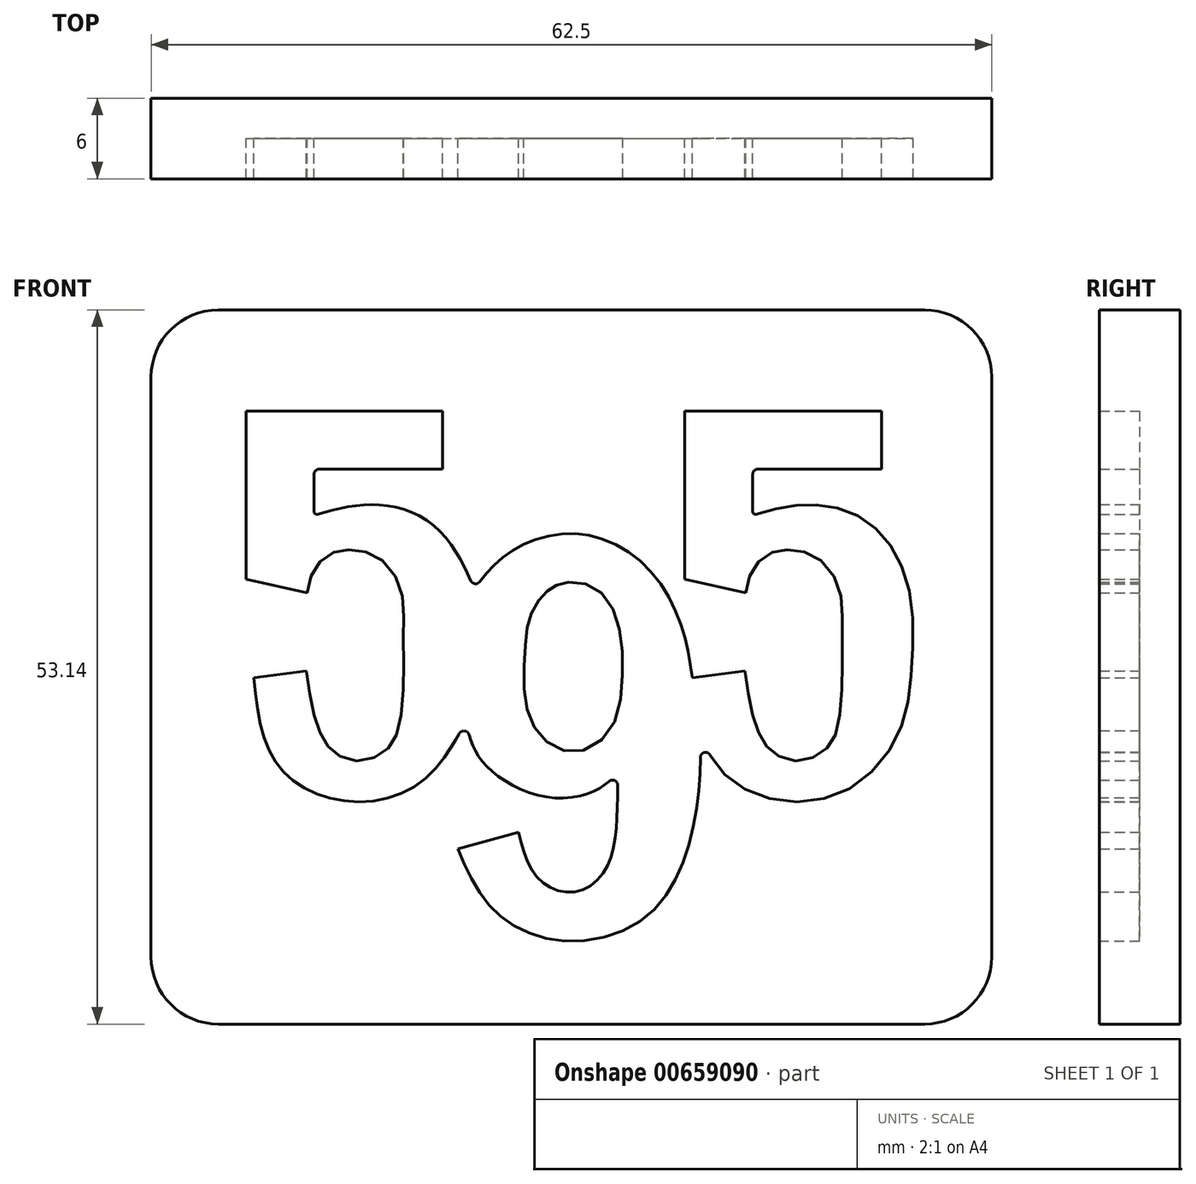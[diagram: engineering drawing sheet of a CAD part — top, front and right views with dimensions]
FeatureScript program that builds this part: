
annotation { "Feature Type Name" : "Feature", "Feature Type Description" : "" }
export const myFeature = defineFeature(function(context is Context, id is Id, definition is map)
    precondition{}
    {
        {
            var Q0;
            Q0=qCreatedBy(makeId("Front.planeOp"),FACE);
            var sketch = newSketch(context, id + "F0", { "sketchPlane" : qUnion([Q0])});
            skLineSegment(sketch, "E0", {"start": v(-24.18, 19.03) * mm, "end": v(-9.57, 19.03) * mm});
            skLineSegment(sketch, "E1", {"start": v(-24.18, 19.03) * mm, "end": v(-24.18, 6.52) * mm});
            skLineSegment(sketch, "E2", {"start": v(-24.18, 6.52) * mm, "end": v(-19.64, 5.52) * mm});
            skLineSegment(sketch, "E3", {"start": v(-9.57, 19.03) * mm, "end": v(-9.57, 14.73) * mm});
            skLineSegment(sketch, "E4", {"start": v(-9.57, 14.73) * mm, "end": v(-18.75, 14.73) * mm});
            skLineSegment(sketch, "E5", {"start": v(-19.13, 14.34) * mm, "end": v(-19.13, 11.56) * mm});
            skLineSegment(sketch, "E6", {"start": v(-19.7, -0.28) * mm, "end": v(-23.62, -0.8) * mm});
            skLineSegment(sketch, "E7", {"start": v(8.43, 19.03) * mm, "end": v(23.04, 19.03) * mm});
            skLineSegment(sketch, "E8", {"start": v(8.43, 19.03) * mm, "end": v(8.43, 6.52) * mm});
            skLineSegment(sketch, "E9", {"start": v(8.43, 6.52) * mm, "end": v(12.97, 5.52) * mm});
            skLineSegment(sketch, "E10", {"start": v(23.04, 19.03) * mm, "end": v(23.04, 14.73) * mm});
            skLineSegment(sketch, "E11", {"start": v(23.04, 14.73) * mm, "end": v(13.87, 14.73) * mm});
            skLineSegment(sketch, "E12", {"start": v(13.48, 14.34) * mm, "end": v(13.48, 11.56) * mm});
            skLineSegment(sketch, "E13", {"start": v(12.9, -0.28) * mm, "end": v(8.99, -0.8) * mm});
            skFitSpline(sketch, "E14", {"points": [v(-23.62, -0.8) * mm, v(-22.6, -5.93) * mm, v(-20.1, -8.86) * mm, v(-15.7, -10.03) * mm, v(-11.16, -8.56) * mm, v(-8.72, -5.62) * mm, v(-8.17, -4.64) * mm], "startDerivative": vector(3.05, -27.84) * mm, "endDerivative": vector(4.84, 9.1) * mm});
            skFitSpline(sketch, "E15", {"points": [v(-19.7, -0.28) * mm, v(-19.17, -3.5) * mm, v(-18.4, -5.44) * mm, v(-17.3, -6.6) * mm, v(-15.43, -6.96) * mm, v(-13.7, -6.12) * mm, v(-12.88, -4.67) * mm, v(-12.49, -0.89) * mm, v(-12.49, 3.08) * mm, v(-12.67, 5.78) * mm, v(-14.23, 8.06) * mm, v(-16.23, 8.7) * mm, v(-17.75, 8.5) * mm, v(-19.11, 7.28) * mm, v(-19.64, 5.52) * mm], "startDerivative": vector(5.37, -39.95) * mm, "endDerivative": vector(-5.42, -28.28) * mm});
            skFitSpline(sketch, "E16", {"points": [v(-19.13, 11.3) * mm, v(-16.5, 11.94) * mm, v(-13.79, 12) * mm, v(-10.94, 11.04) * mm, v(-8.67, 8.72) * mm, v(-7.35, 6.14) * mm], "startDerivative": vector(13.56, 3.87) * mm, "endDerivative": vector(5.77, -13.07) * mm});
            skFitSpline(sketch, "E17", {"points": [v(12.9, -0.28) * mm, v(13.45, -3.5) * mm, v(14.2, -5.44) * mm, v(15.31, -6.6) * mm, v(17.18, -6.96) * mm, v(18.92, -6.12) * mm, v(19.73, -4.67) * mm, v(20.13, -0.89) * mm, v(20.13, 3.08) * mm, v(19.94, 5.78) * mm, v(18.38, 8.06) * mm, v(16.39, 8.7) * mm, v(14.87, 8.5) * mm, v(13.5, 7.28) * mm, v(12.97, 5.52) * mm], "startDerivative": vector(5.37, -39.95) * mm, "endDerivative": vector(-5.42, -28.28) * mm});
            skFitSpline(sketch, "E18", {"points": [v(13.48, 11.3) * mm, v(16.1, 11.94) * mm, v(18.82, 12) * mm, v(21.67, 11.04) * mm, v(23.94, 8.72) * mm, v(25.26, 4.86) * mm, v(25.26, -0.53) * mm, v(24.45, -4.64) * mm, v(21.45, -8.56) * mm, v(16.92, -10.03) * mm, v(12.52, -8.86) * mm, v(10, -5.93) * mm, v(8.99, -0.8) * mm], "startDerivative": vector(38.15, 10.87) * mm, "endDerivative": vector(-6.34, 57.7) * mm});
            skFitSpline(sketch, "E19", {"points": [v(-6.99, 6.14) * mm, v(-5.14, 8.11) * mm, v(-2.12, 9.65) * mm, v(1.76, 9.7) * mm, v(5.68, 7.36) * mm, v(8.15, 3.12) * mm, v(8.99, -0.8) * mm], "startDerivative": vector(11.95, 14.85) * mm, "endDerivative": vector(3.37, -22.8) * mm});
            skFitSpline(sketch, "E20", {"points": [v(-7.74, -4.64) * mm, v(-7.12, -6.3) * mm, v(-5.44, -8.13) * mm, v(-1.75, -9.7) * mm, v(1.6, -9.28) * mm, v(3.17, -8.19) * mm], "startDerivative": vector(2.95, -10.23) * mm, "endDerivative": vector(7.99, 7.04) * mm});
            skFitSpline(sketch, "E21", {"points": [v(3.44, -8.19) * mm, v(3.33, -11.92) * mm, v(2.71, -14.7) * mm, v(1, -16.53) * mm, v(-1.13, -16.6) * mm, v(-2.87, -15.22) * mm, v(-3.92, -12.3) * mm], "startDerivative": vector(-0.15, -19.77) * mm, "endDerivative": vector(-4.54, 17.97) * mm});
            skLineSegment(sketch, "E22", {"start": v(-3.92, -12.3) * mm, "end": v(-8.44, -13.55) * mm});
            skFitSpline(sketch, "E23", {"points": [v(-8.44, -13.55) * mm, v(-6.76, -16.9) * mm, v(-4.1, -19.34) * mm, v(0.43, -20.41) * mm, v(5.52, -18.63) * mm, v(8.22, -14.7) * mm, v(9.4, -9.92) * mm, v(9.6, -5.93) * mm], "startDerivative": vector(11.35, -26.69) * mm, "endDerivative": vector(0.32, 28.6) * mm});
            skFitSpline(sketch, "E24", {"points": [v(-3.44, 1.62) * mm, v(-3.47, -2.1) * mm, v(-2.47, -4.9) * mm, v(0, -6.32) * mm, v(2.83, -4.74) * mm, v(3.8, -0.57) * mm, v(3.41, 3.45) * mm, v(1.7, 5.91) * mm, v(-0.47, 6.28) * mm, v(-1.4, 5.92) * mm, v(-2.26, 5.2) * mm, v(-3.07, 3.73) * mm, v(-3.44, 1.62) * mm]});
            skArc(sketch, "E25.filletArc", {"start": v(-19.13, 11.56) * mm, "mid": v(-19.05, 11.4) * mm, "end": v(-18.88, 11.37) * mm});
            skArc(sketch, "E26.filletArc", {"start": v(-7.48, 6.42) * mm, "mid": v(-7.18, 6.2) * mm, "end": v(-6.83, 6.34) * mm});
            skArc(sketch, "E27.filletArc", {"start": v(-7.62, -5.03) * mm, "mid": v(-7.95, -4.76) * mm, "end": v(-8.33, -4.96) * mm});
            skArc(sketch, "E28.filletArc", {"start": v(3.44, -8.8) * mm, "mid": v(3.22, -8.45) * mm, "end": v(2.8, -8.5) * mm});
            skArc(sketch, "E29.filletArc", {"start": v(13.48, 11.56) * mm, "mid": v(13.56, 11.4) * mm, "end": v(13.73, 11.37) * mm});
            skPoint(sketch, "E30.visualSharp", {"position": v(13.48, 14.73) * mm});
            skArc(sketch, "E30.filletArc", {"start": v(13.87, 14.73) * mm, "mid": v(13.6, 14.61) * mm, "end": v(13.48, 14.34) * mm});
            skPoint(sketch, "E31.visualSharp", {"position": v(-19.13, 14.73) * mm});
            skArc(sketch, "E31.filletArc", {"start": v(-18.75, 14.73) * mm, "mid": v(-19.02, 14.61) * mm, "end": v(-19.13, 14.34) * mm});
            skArc(sketch, "E32.filletArc", {"start": v(10.3, -6.55) * mm, "mid": v(9.88, -6.36) * mm, "end": v(9.58, -6.73) * mm});
            skLineSegment(sketch, "E33.bottom", {"start": v(26.25, -26.57) * mm, "end": v(-26.25, -26.57) * mm});
            skLineSegment(sketch, "E33.top", {"start": v(26.25, 26.57) * mm, "end": v(-26.25, 26.57) * mm});
            skLineSegment(sketch, "E33.left", {"start": v(31.25, -21.57) * mm, "end": v(31.25, 21.57) * mm});
            skLineSegment(sketch, "E33.right", {"start": v(-31.25, -21.57) * mm, "end": v(-31.25, 21.57) * mm});
            skPoint(sketch, "E33.middle", {"position": v(0, 0) * mm});
            skPoint(sketch, "E34.visualSharp", {"position": v(-31.25, 26.57) * mm});
            skArc(sketch, "E34.filletArc", {"start": v(-26.25, 26.57) * mm, "mid": v(-29.79, 25.1) * mm, "end": v(-31.25, 21.57) * mm});
            skPoint(sketch, "E35.visualSharp", {"position": v(-31.25, -26.57) * mm});
            skArc(sketch, "E35.filletArc", {"start": v(-31.25, -21.57) * mm, "mid": v(-29.79, -25.1) * mm, "end": v(-26.25, -26.57) * mm});
            skPoint(sketch, "E36.visualSharp", {"position": v(31.25, -26.57) * mm});
            skArc(sketch, "E36.filletArc", {"start": v(26.25, -26.57) * mm, "mid": v(29.79, -25.1) * mm, "end": v(31.25, -21.57) * mm});
            skPoint(sketch, "E37.visualSharp", {"position": v(31.25, 26.57) * mm});
            skArc(sketch, "E37.filletArc", {"start": v(31.25, 21.57) * mm, "mid": v(29.79, 25.1) * mm, "end": v(26.25, 26.57) * mm});
            skSolve(sketch);
        }
        {
            var Q0;
            Q0=makeQuery(id+"F0.imprint","IMPRINT",FACE,{"disambiguationData":[TD([[makeQuery(id+"F0.imprint","IMPRINT",EDGE,{"derivedFrom":sQuery(id+"F0.wireOp",EDGE,"E0")}),1.0]])]});
            var Q1;
            Q1=makeQuery(id+"F0.imprint","IMPRINT",FACE,{"disambiguationData":[TD([[makeQuery(id+"F0.imprint","IMPRINT",EDGE,{"derivedFrom":sQuery(id+"F0.wireOp",EDGE,"E24")}),1.0]])]});
            extrude(context, id + "F1", {"entities" : qUnion([Q0, Q1]), "depth" : 3 * mm, "offsetDistance" : 25 * mm});
        }
        {
            var Q0;
            Q0=makeQuery(id+"F0.imprint","IMPRINT",FACE,{"disambiguationData":[TD([[makeQuery(id+"F0.imprint","IMPRINT",EDGE,{"derivedFrom":sQuery(id+"F0.wireOp",EDGE,"E0")}),1.0]])]});
            var sketch = newSketch(context, id + "F2", { "sketchPlane" : qUnion([Q0])});
            skArc(sketch, "E38.0.0", {"start": v(31.25, 21.57) * mm, "mid": v(29.79, 25.1) * mm, "end": v(26.25, 26.57) * mm});
            skLineSegment(sketch, "E38.0.1", {"start": v(26.25, 26.57) * mm, "end": v(-26.25, 26.57) * mm});
            skArc(sketch, "E38.0.2", {"start": v(-26.25, 26.57) * mm, "mid": v(-29.79, 25.1) * mm, "end": v(-31.25, 21.57) * mm});
            skLineSegment(sketch, "E38.0.3", {"start": v(-31.25, 21.57) * mm, "end": v(-31.25, -21.57) * mm});
            skArc(sketch, "E38.0.4", {"start": v(-31.25, -21.57) * mm, "mid": v(-29.79, -25.1) * mm, "end": v(-26.25, -26.57) * mm});
            skLineSegment(sketch, "E38.0.5", {"start": v(-26.25, -26.57) * mm, "end": v(26.25, -26.57) * mm});
            skArc(sketch, "E38.0.6", {"start": v(26.25, -26.57) * mm, "mid": v(29.79, -25.1) * mm, "end": v(31.25, -21.57) * mm});
            skLineSegment(sketch, "E38.0.7", {"start": v(31.25, -21.57) * mm, "end": v(31.25, 21.57) * mm});
            skSolve(sketch);
        }
        {
            var Q0;
            Q0 = qSketchRegion(id + "F2", true);
            extrude(context, id + "F3", {"entities" : qUnion([Q0]), "operationType" : NewBodyOperationType.ADD, "oppositeDirection" : true, "depth" : 3 * mm, "offsetDistance" : 25 * mm});
        }
    });
